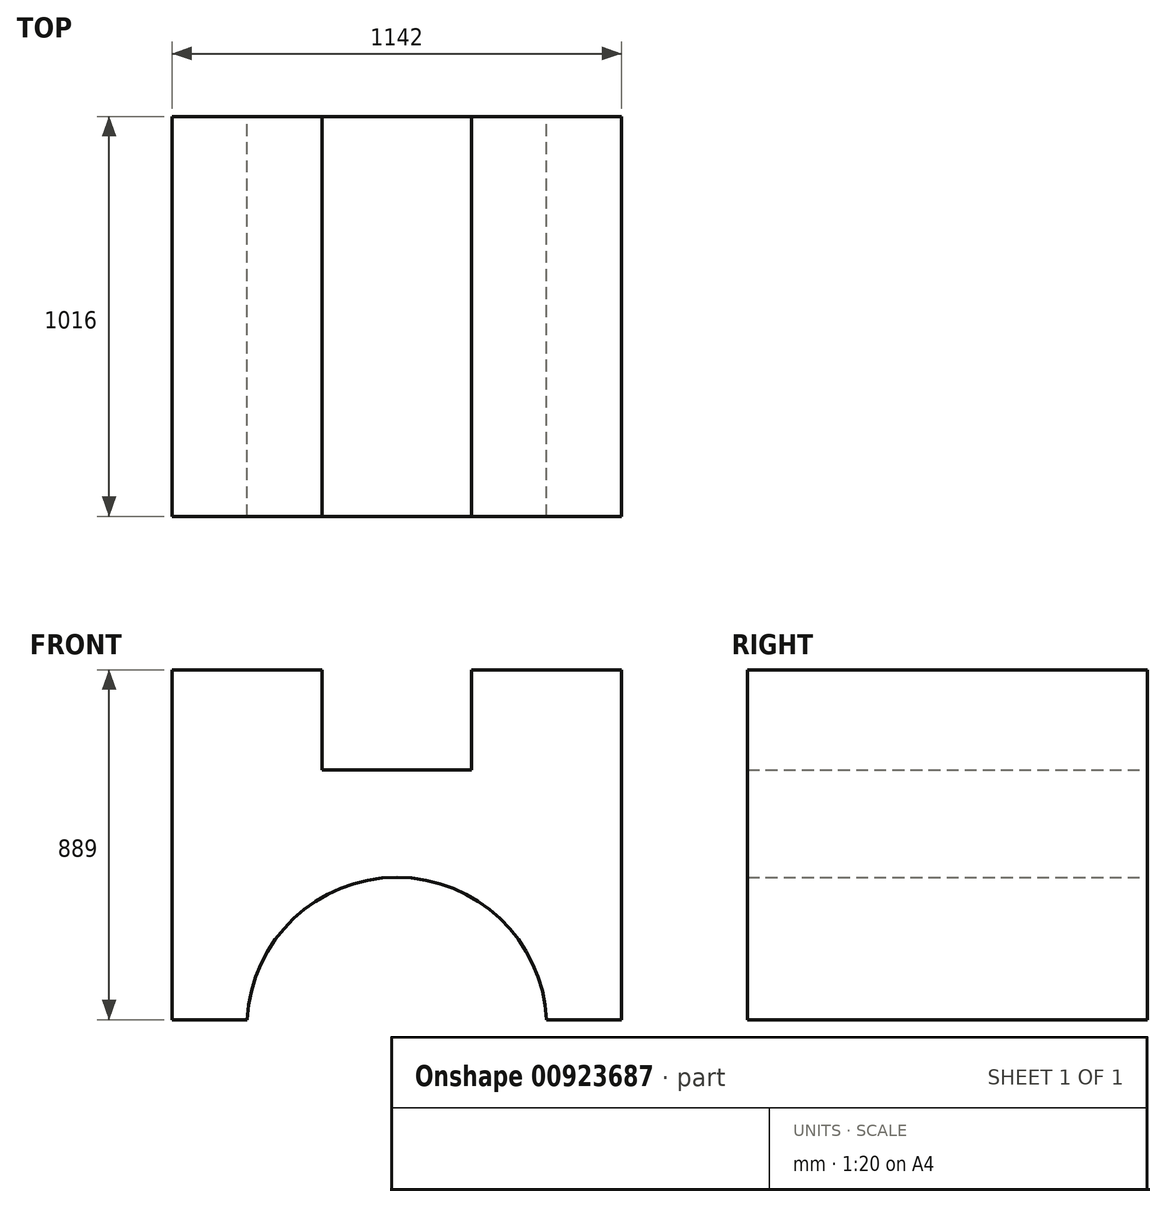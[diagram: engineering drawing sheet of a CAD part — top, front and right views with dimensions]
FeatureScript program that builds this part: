
annotation { "Feature Type Name" : "Feature", "Feature Type Description" : "" }
export const myFeature = defineFeature(function(context is Context, id is Id, definition is map)
    precondition{}
    {
        {
            var Q0;
            Q0=qCreatedBy(makeId("Front.planeOp"),FACE);
            var sketch = newSketch(context, id + "F0", { "sketchPlane" : qUnion([Q0])});
            skLineSegment(sketch, "E0.bottom", {"start": v(-571, 444.5) * mm, "end": v(-190, 444.5) * mm});
            skLineSegment(sketch, "E0.top", {"start": v(-571, -444.5) * mm, "end": v(-380.5, -444.5) * mm});
            skLineSegment(sketch, "E0.left", {"start": v(-571, 444.5) * mm, "end": v(-571, -444.5) * mm});
            skLineSegment(sketch, "E0.right", {"start": v(571, 444.5) * mm, "end": v(571, -444.5) * mm});
            skPoint(sketch, "E0.middle", {"position": v(0, 0) * mm});
            skLineSegment(sketch, "E1.top", {"start": v(-190, 190.5) * mm, "end": v(190, 190.5) * mm});
            skLineSegment(sketch, "E1.left", {"start": v(-190, 444.5) * mm, "end": v(-190, 190.5) * mm});
            skLineSegment(sketch, "E1.right", {"start": v(190, 444.5) * mm, "end": v(190, 190.5) * mm});
            skLineSegment(sketch, "E2.trimOffspring", {"start": v(190, 444.5) * mm, "end": v(571, 444.5) * mm});
            skArc(sketch, "E3", {"start": v(380.5, -444.5) * mm, "mid": v(0, -82.97) * mm, "end": v(-380.5, -444.5) * mm});
            skLineSegment(sketch, "E4.trimOffspring", {"start": v(380.5, -444.5) * mm, "end": v(571, -444.5) * mm});
            skSolve(sketch);
        }
        {
            var Q0;
            Q0=makeQuery(id+"F0.imprint","IMPRINT",FACE,{"disambiguationData":[TD([[makeQuery(id+"F0.imprint","IMPRINT",EDGE,{"derivedFrom":sQuery(id+"F0.wireOp",EDGE,"E0.bottom")}),-1.0]])]});
            extrude(context, id + "F1", {"entities" : qUnion([Q0]), "depth" : 1016 * mm, "offsetDistance" : 25.4 * mm});
        }
    });
